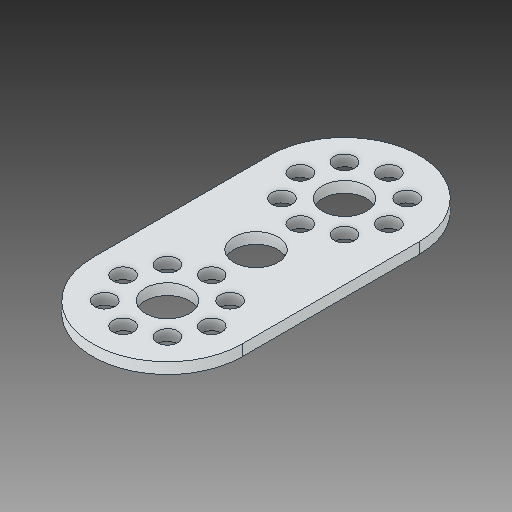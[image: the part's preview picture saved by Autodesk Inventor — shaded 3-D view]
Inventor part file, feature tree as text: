
AUTODESK INVENTOR PART (.ipt)
format: ipt  version: 2018 (Build 220112000, 112)  size: 166,912 bytes
history: native  units: in
note: dims shown in document units (in); Inventor stores cm internally (conversion verified against a paired STEP export)
features: extrude x1
ambient origin geometry x8: Origin, YZ Plane, XZ Plane, XY Plane, X Axis, Y Axis, Z Axis, Center Point
bodies: Solid1 (feature_tree)
feature tree (1):
  extrude  "Extrude2"  [1 undecoded]
note: 1 required parameter value undecoded (feature->parameter linkage not recoverable at this tier; creation-order binding heuristic only, values carry confidence <= 0.55)
